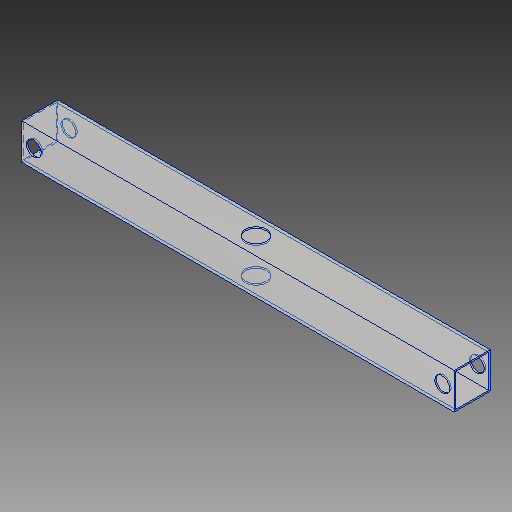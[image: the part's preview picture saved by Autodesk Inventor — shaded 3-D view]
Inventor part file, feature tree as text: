
AUTODESK INVENTOR PART (.ipt)
format: ipt  version: 2019 (Build 230136000, 136)  size: 121,344 bytes
history: native  units: in
note: dims shown in document units (in); Inventor stores cm internally (conversion verified against a paired STEP export)
features: extrude x3, sketch x3
ambient origin geometry x8: Origin, YZ Plane, XZ Plane, XY Plane, X Axis, Y Axis, Z Axis, Center Point
bodies: Solid1 (feature_tree)
feature tree (6):
  extrude  "Extrusion1"  Depth=1.5in
  extrude  "Extrusion2"  Depth=18.0in
  extrude  "Extrusion4"  Depth=15.0in TaperAngle=0.0deg
  sketch  "Sketch2"  dims[d0=0.0625in d1=1.5in]
  sketch  "Sketch3"  dims[d2=18.0in d3=0.0in d4=0.5in]
  sketch  "Sketch5"  dims[d5=0.625in d6=15.0in d7=0.0in d11=0.875in d12=1.0in d13=0.0in]
